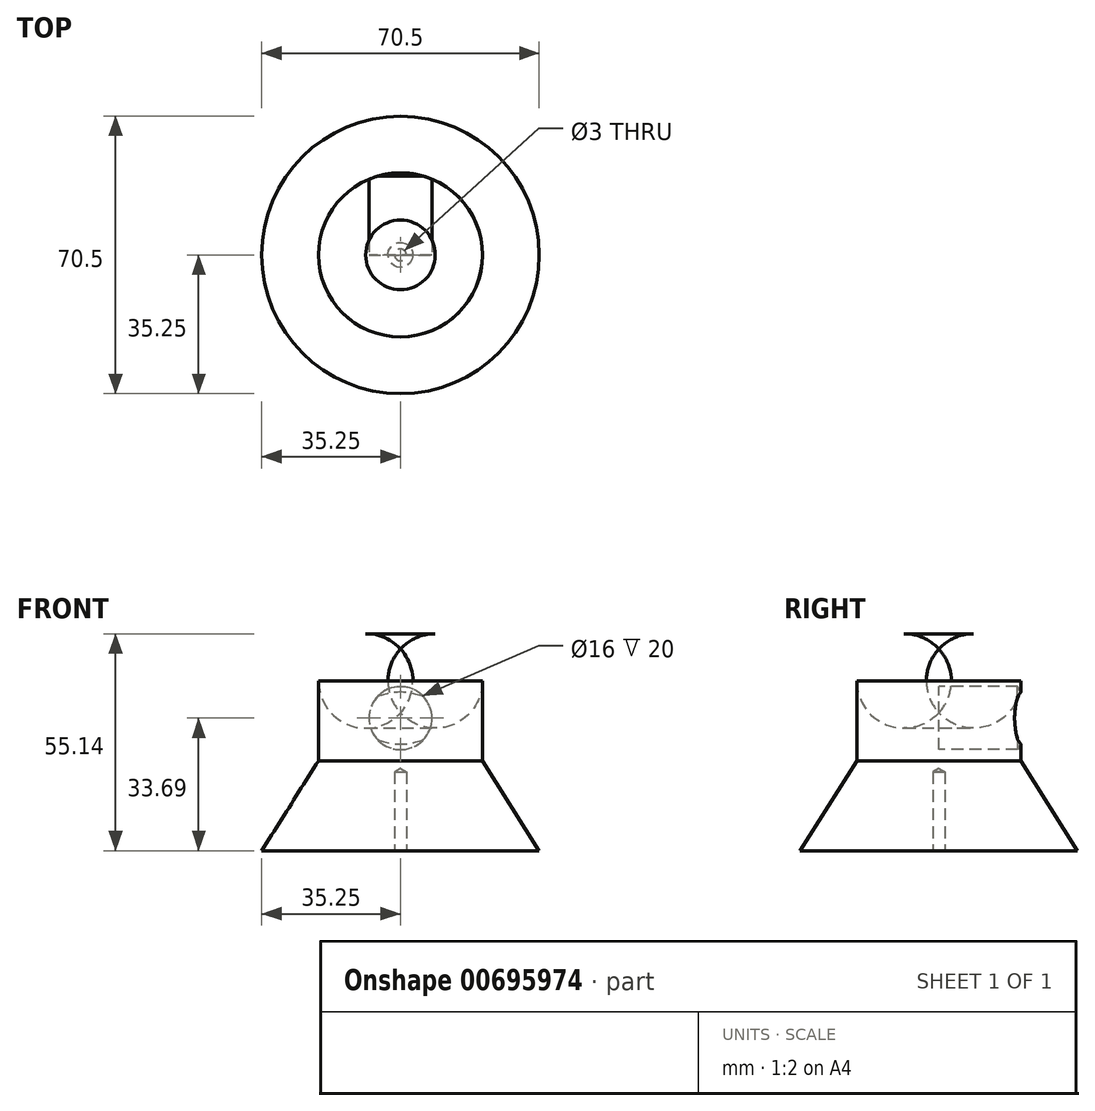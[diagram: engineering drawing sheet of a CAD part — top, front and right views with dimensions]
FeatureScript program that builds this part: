
annotation { "Feature Type Name" : "Feature", "Feature Type Description" : "" }
export const myFeature = defineFeature(function(context is Context, id is Id, definition is map)
    precondition{}
    {
        {
            var Q0;
            Q0=qCreatedBy(makeId("Front.planeOp"),FACE);
            var sketch = newSketch(context, id + "F0", { "sketchPlane" : qUnion([Q0])});
            skLineSegment(sketch, "E0", {"start": v(0, 0) * mm, "end": v(0, 55.14) * mm});
            skLineSegment(sketch, "E1", {"start": v(0, 0) * mm, "end": v(35.25, 0) * mm});
            skLineSegment(sketch, "E2", {"start": v(0, 55.14) * mm, "end": v(8.84, 55.14) * mm});
            skLineSegment(sketch, "E3", {"start": v(35.25, 0) * mm, "end": v(20.84, 22.87) * mm});
            skLineSegment(sketch, "E4", {"start": v(20.84, 22.87) * mm, "end": v(20.84, 43.14) * mm});
            skPoint(sketch, "E5.visualSharp", {"position": v(20.84, 55.14) * mm});
            skArc(sketch, "E5.filletArc", {"start": v(20.84, 43.14) * mm, "mid": v(17.32, 51.63) * mm, "end": v(8.84, 55.14) * mm});
            skSolve(sketch);
        }
        {
            var Q0;
            Q0=makeQuery(id+"F0.imprint","IMPRINT",FACE,{"disambiguationData":[TD([[makeQuery(id+"F0.imprint","IMPRINT",EDGE,{"derivedFrom":sQuery(id+"F0.wireOp",EDGE,"E0")}),-1.0]])]});
            var Q1;
            Q1=sQuery(id+"F0.wireOp",EDGE,"E0");
            var Q2;
            Q2=sQuery(id+"F0.wireOp",EDGE,"E0");
            revolve(context, id + "F1", {"entities" : qUnion([Q0]), "surfaceEntities" : qUnion([Q1]), "axis" : qUnion([Q2]), "revolveType" : RevolveType.FULL});
        }
        {
            var Q0;
            Q0=qCreatedBy(makeId("Front.planeOp"),FACE);
            var sketch = newSketch(context, id + "F2", { "sketchPlane" : qUnion([Q0])});
            skPoint(sketch, "E6", {"position": v(0, 33.69) * mm});
            skSolve(sketch);
        }
        {
            var Q0;
            Q0=sQuery(id+"F2.wireOp",VERTEX,"E6");
            var Q1;
            Q1=makeQuery(id+"F1.opRevolve","SWEPT_BODY",BODY,{"disambiguationData":[OSD([sQuery(id+"F0.wireOp",EDGE,"E0"),sQuery(id+"F0.wireOp",EDGE,"E1"),sQuery(id+"F0.wireOp",EDGE,"E2"),sQuery(id+"F0.wireOp",EDGE,"E3"),sQuery(id+"F0.wireOp",EDGE,"E4"),sQuery(id+"F0.wireOp",EDGE,"E5.filletArc")])]});
            hole(context, id + "F3", {"style" : HoleStyle.C_BORE, "endStyle" : HoleEndStyle.BLIND, "holeDiameter" : 16 * mm, "cBoreDiameter" : 16 * mm, "cBoreDepth" : 20 * mm, "majorDiameter" : 5 * mm, "holeDepth" : 20 * mm, "isTappedThrough" : true, "tappedDepth" : 12 * mm, "tapClearance" : 3, "locations" : qUnion([Q0]), "scope" : qUnion([Q1])});
        }
        {
            var Q0;
            Q0=makeQuery(id+"F1.opRevolve","SWEPT_FACE",FACE,{"disambiguationData":[OSD([sQuery(id+"F0.wireOp",EDGE,"E1")])]});
            var sketch = newSketch(context, id + "F4", { "sketchPlane" : qUnion([Q0])});
            skPoint(sketch, "E7", {"position": v(0, 0) * mm});
            skSolve(sketch);
        }
        {
            var Q0;
            Q0=sQuery(id+"F4.wireOp",VERTEX,"E7");
            var Q1;
            Q1=makeQuery(id+"F1.opRevolve","SWEPT_BODY",BODY,{"disambiguationData":[OSD([sQuery(id+"F0.wireOp",EDGE,"E0"),sQuery(id+"F0.wireOp",EDGE,"E1"),sQuery(id+"F0.wireOp",EDGE,"E2"),sQuery(id+"F0.wireOp",EDGE,"E3"),sQuery(id+"F0.wireOp",EDGE,"E4"),sQuery(id+"F0.wireOp",EDGE,"E5.filletArc")])]});
            hole(context, id + "F5", {"style" : HoleStyle.SIMPLE, "endStyle" : HoleEndStyle.BLIND, "holeDiameter" : 3 * mm, "majorDiameter" : 5 * mm, "holeDepth" : 20 * mm, "isTappedThrough" : true, "tappedDepth" : 12 * mm, "tapClearance" : 3, "startFromSketch" : true, "locations" : qUnion([Q0]), "scope" : qUnion([Q1])});
        }
    });
